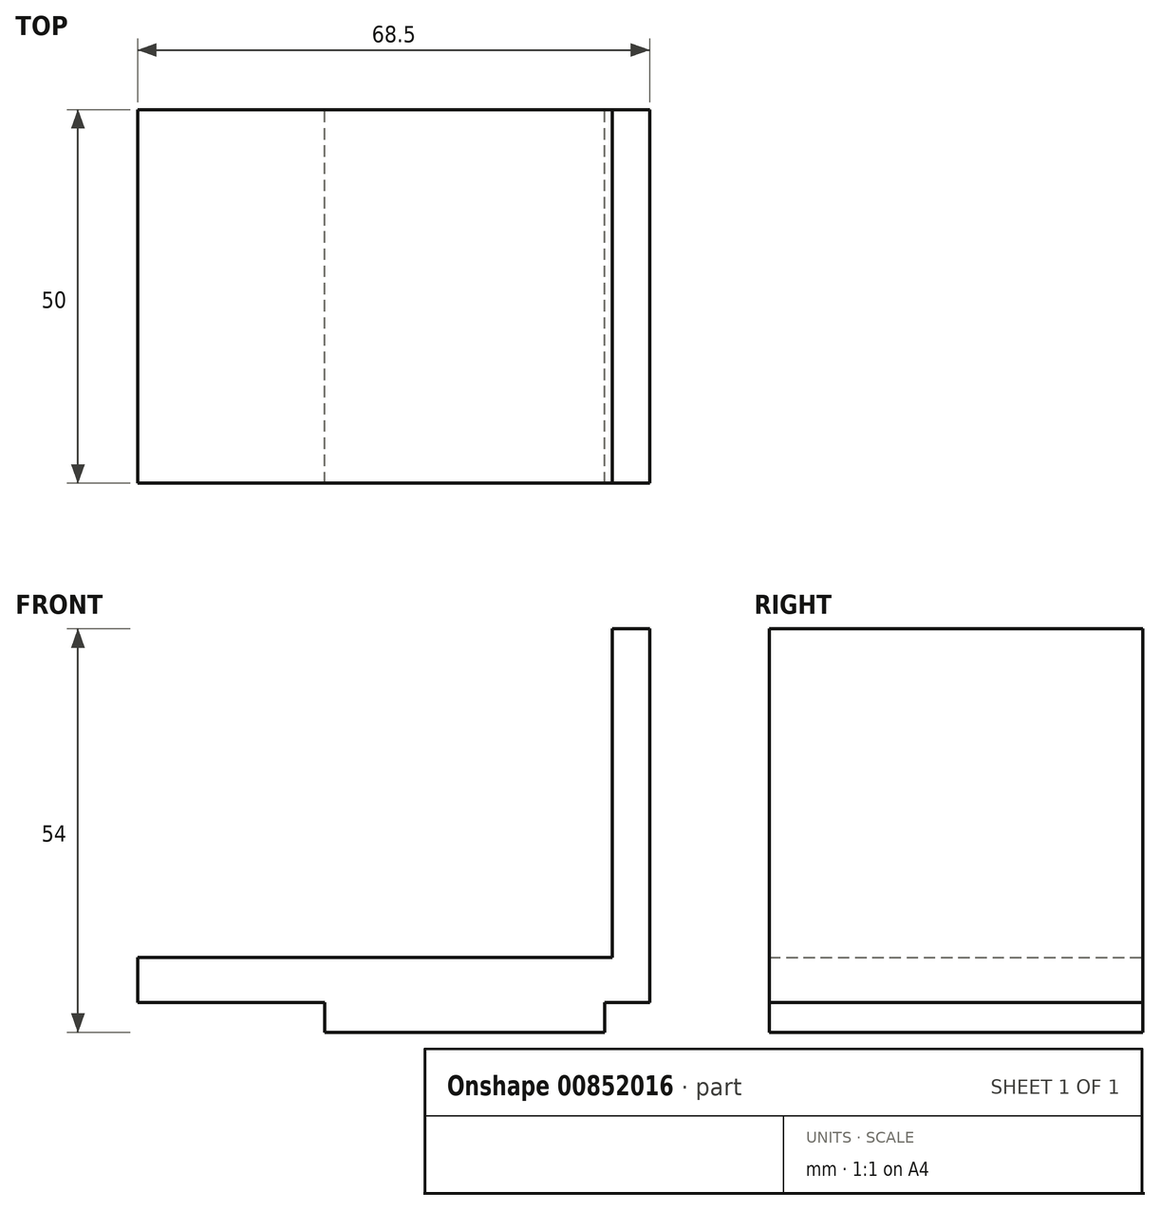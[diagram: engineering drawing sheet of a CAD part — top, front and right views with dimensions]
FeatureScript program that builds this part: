
annotation { "Feature Type Name" : "Feature", "Feature Type Description" : "" }
export const myFeature = defineFeature(function(context is Context, id is Id, definition is map)
    precondition{}
    {
        {
            var Q0;
            Q0=qCreatedBy(makeId("Front.planeOp"),FACE);
            var sketch = newSketch(context, id + "F0", { "sketchPlane" : qUnion([Q0])});
            skLineSegment(sketch, "E0", {"start": v(0, 0) * mm, "end": v(0, -6) * mm});
            skLineSegment(sketch, "E1", {"start": v(0, -6) * mm, "end": v(25, -6) * mm});
            skLineSegment(sketch, "E2", {"start": v(25, -6) * mm, "end": v(25, -10) * mm});
            skLineSegment(sketch, "E3", {"start": v(25, -10) * mm, "end": v(62.5, -10) * mm});
            skLineSegment(sketch, "E4", {"start": v(62.5, -10) * mm, "end": v(62.5, -6) * mm});
            skLineSegment(sketch, "E5", {"start": v(62.5, -6) * mm, "end": v(68.5, -6) * mm});
            skLineSegment(sketch, "E6", {"start": v(68.5, -6) * mm, "end": v(68.5, 44) * mm});
            skLineSegment(sketch, "E7", {"start": v(68.5, 44) * mm, "end": v(63.5, 44) * mm});
            skLineSegment(sketch, "E8", {"start": v(63.5, 44) * mm, "end": v(63.5, 0) * mm});
            skLineSegment(sketch, "E9", {"start": v(63.5, 0) * mm, "end": v(0, 0) * mm});
            skSolve(sketch);
        }
        {
            var Q0;
            Q0=makeQuery(id+"F0.imprint","IMPRINT",FACE,{"disambiguationData":[TD([[makeQuery(id+"F0.imprint","IMPRINT",EDGE,{"derivedFrom":sQuery(id+"F0.wireOp",EDGE,"E0")}),1.0]])]});
            extrude(context, id + "F1", {"entities" : qUnion([Q0]), "depth" : 50 * mm, "offsetDistance" : 25 * mm});
        }
    });
